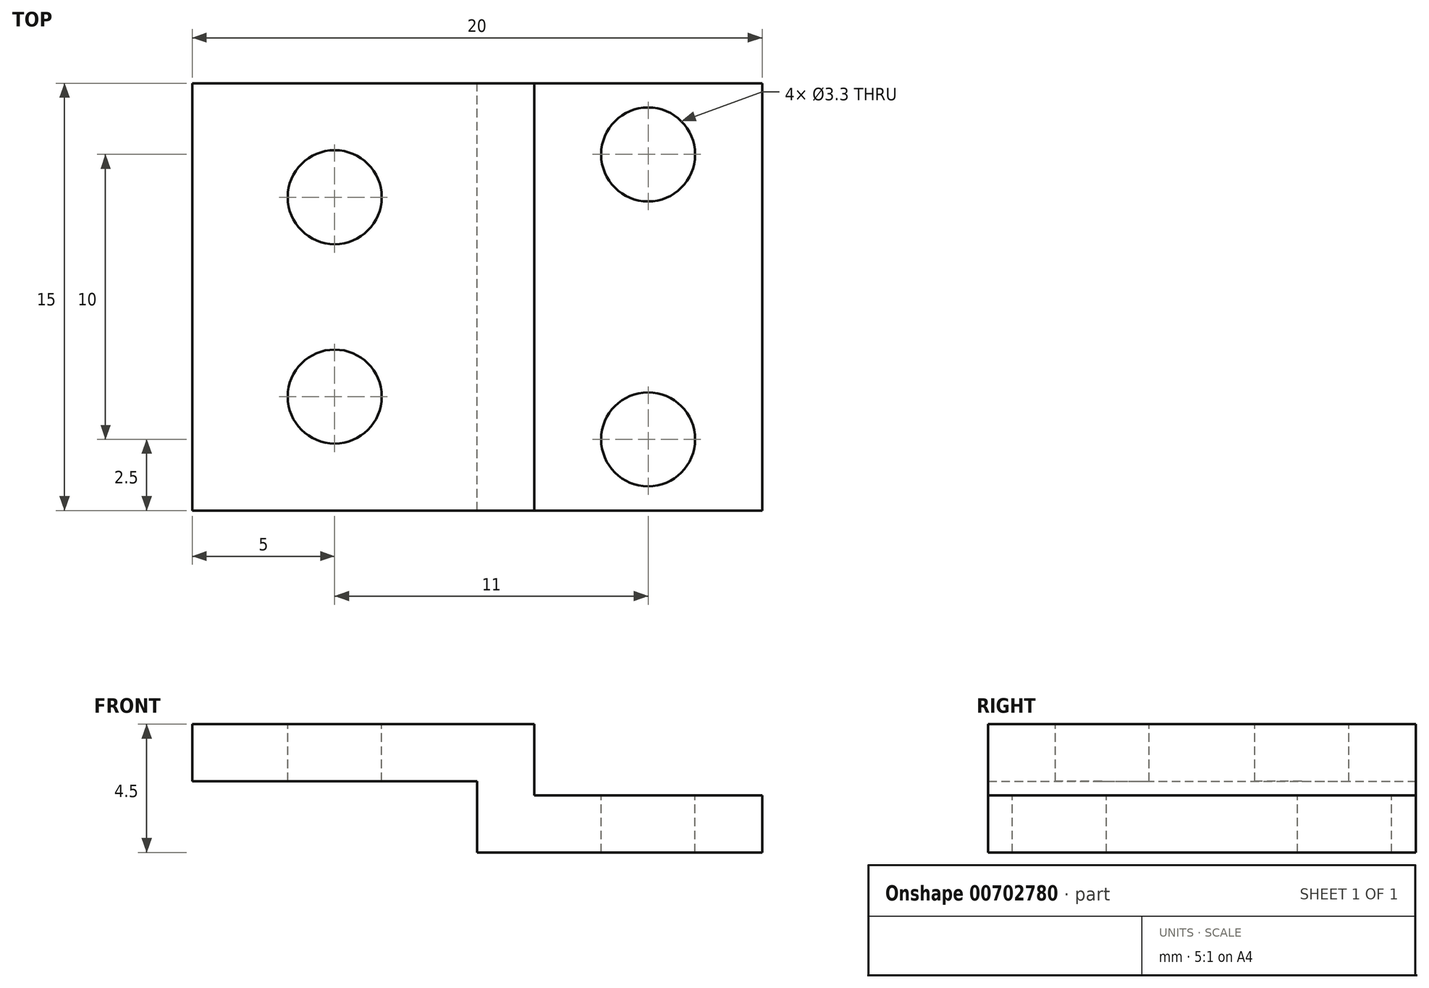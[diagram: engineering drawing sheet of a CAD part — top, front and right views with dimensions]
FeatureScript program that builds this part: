
annotation { "Feature Type Name" : "Feature", "Feature Type Description" : "" }
export const myFeature = defineFeature(function(context is Context, id is Id, definition is map)
    precondition{}
    {
        {
            var Q0;
            Q0=qCreatedBy(makeId("Front.planeOp"),FACE);
            var sketch = newSketch(context, id + "F0", { "sketchPlane" : qUnion([Q0])});
            skLineSegment(sketch, "E0", {"start": v(0, 0) * mm, "end": v(-8, 0) * mm});
            skLineSegment(sketch, "E1", {"start": v(-8, 0) * mm, "end": v(-8, 2.5) * mm});
            skLineSegment(sketch, "E2", {"start": v(-8, 2.5) * mm, "end": v(-20, 2.5) * mm});
            skLineSegment(sketch, "E3.0", {"start": v(-10, 0.5) * mm, "end": v(-20, 0.5) * mm});
            skLineSegment(sketch, "E3.1", {"start": v(-10, -2) * mm, "end": v(-10, 0.5) * mm});
            skLineSegment(sketch, "E3.2", {"start": v(0, -2) * mm, "end": v(-10, -2) * mm});
            skLineSegment(sketch, "E4", {"start": v(-20, 2.5) * mm, "end": v(-20, 0.5) * mm});
            skLineSegment(sketch, "E5", {"start": v(0, -2) * mm, "end": v(0, 0) * mm});
            skSolve(sketch);
        }
        {
            var Q0;
            Q0 = qSketchRegion(id + "F0", true);
            extrude(context, id + "F1", {"entities" : qUnion([Q0]), "endBound" : BoundingType.SYMMETRIC, "depth" : 15 * mm, "offsetDistance" : 25 * mm});
        }
        {
            var Q0;
            Q0=makeQuery(id+"F1.opExtrude","SWEPT_FACE",FACE,{"disambiguationData":[OSD([sQuery(id+"F0.wireOp",EDGE,"E2")])]});
            var sketch = newSketch(context, id + "F2", { "sketchPlane" : qUnion([Q0])});
            skLineSegment(sketch, "E6", {"start": v(-20, 7.5) * mm, "end": v(-20, -7.5) * mm});
            skLineSegment(sketch, "E7", {"start": v(-20, 0) * mm, "end": v(-8, 0) * mm, "construction": true});
            skLineSegment(sketch, "E8", {"start": v(-20, -3.5) * mm, "end": v(-8, -3.5) * mm, "construction": true});
            skLineSegment(sketch, "E9", {"start": v(-15, -7.5) * mm, "end": v(-15, 7.5) * mm, "construction": true});
            skCircle(sketch, "E10", {"center": v(-15, -3.5) * mm, "radius": 1.55 * mm, "construction": true});
            skCircle(sketch, "E11.MirrorC", {"center": v(-15, 3.5) * mm, "radius": 1.55 * mm, "construction": true});
            skLineSegment(sketch, "E12.MirrorCS", {"start": v(-20, 3.5) * mm, "end": v(-8, 3.5) * mm, "construction": true});
            skSolve(sketch);
        }
        {
            var Q0;
            Q0=sQuery(id+"F2.wireOp",VERTEX,"E10.center");
            var Q1;
            Q1=sQuery(id+"F2.wireOp",VERTEX,"E11.MirrorC.center");
            var Q2;
            Q2=makeQuery(id+"F1.opExtrude","SWEPT_BODY",BODY,{"disambiguationData":[OSD([sQuery(id+"F0.wireOp",EDGE,"E0"),sQuery(id+"F0.wireOp",EDGE,"E1"),sQuery(id+"F0.wireOp",EDGE,"E2"),sQuery(id+"F0.wireOp",EDGE,"E3.0"),sQuery(id+"F0.wireOp",EDGE,"E3.1"),sQuery(id+"F0.wireOp",EDGE,"E3.2"),sQuery(id+"F0.wireOp",EDGE,"E4"),sQuery(id+"F0.wireOp",EDGE,"E5")])]});
            hole(context, id + "F3", {"style" : HoleStyle.SIMPLE, "endStyle" : HoleEndStyle.THROUGH, "standardTappedOrClearance" : lookupTablePath({ "standard" : "ISO", "fit" : "Normal", "size" : "M3", "type" : "Clearance" }), "standardBlindInLast" : lookupTablePath({ "fit" : "Standard", "standard" : "ISO", "size" : "M3", "type" : "Clearance" }), "holeDiameter" : 3.3 * mm, "majorDiameter" : 5 * mm, "isTappedThrough" : true, "tappedDepth" : 12 * mm, "tapClearance" : 3, "locations" : qUnion([Q0, Q1]), "scope" : qUnion([Q2])});
        }
        {
            var Q0;
            Q0=makeQuery(id+"F1.opExtrude","SWEPT_FACE",FACE,{"disambiguationData":[OSD([sQuery(id+"F0.wireOp",EDGE,"E0")])]});
            var sketch = newSketch(context, id + "F4", { "sketchPlane" : qUnion([Q0])});
            skLineSegment(sketch, "E13", {"start": v(0, -7.5) * mm, "end": v(0, 7.5) * mm, "construction": true});
            skLineSegment(sketch, "E14.0", {"start": v(-4, -7.5) * mm, "end": v(-4, 7.5) * mm, "construction": true});
            skLineSegment(sketch, "E15", {"start": v(0, 0) * mm, "end": v(-8, 0) * mm, "construction": true});
            skLineSegment(sketch, "E16", {"start": v(0, -5) * mm, "end": v(-7.64, -5) * mm, "construction": true});
            skCircle(sketch, "E17", {"center": v(-4, -5) * mm, "radius": 1.55 * mm, "construction": true});
            skCircle(sketch, "E18.MirrorC", {"center": v(-4, 5) * mm, "radius": 1.55 * mm, "construction": true});
            skLineSegment(sketch, "E19.MirrorCS", {"start": v(0, 5) * mm, "end": v(-7.64, 5) * mm, "construction": true});
            skSolve(sketch);
        }
        {
            var Q0;
            Q0=sQuery(id+"F4.wireOp",VERTEX,"E17.center");
            var Q1;
            Q1=sQuery(id+"F4.wireOp",VERTEX,"E18.MirrorC.center");
            var Q2;
            Q2=makeQuery(id+"F1.opExtrude","SWEPT_BODY",BODY,{"disambiguationData":[OSD([sQuery(id+"F0.wireOp",EDGE,"E0"),sQuery(id+"F0.wireOp",EDGE,"E1"),sQuery(id+"F0.wireOp",EDGE,"E2"),sQuery(id+"F0.wireOp",EDGE,"E3.0"),sQuery(id+"F0.wireOp",EDGE,"E3.1"),sQuery(id+"F0.wireOp",EDGE,"E3.2"),sQuery(id+"F0.wireOp",EDGE,"E4"),sQuery(id+"F0.wireOp",EDGE,"E5")])]});
            hole(context, id + "F5", {"style" : HoleStyle.SIMPLE, "endStyle" : HoleEndStyle.THROUGH, "standardTappedOrClearance" : lookupTablePath({ "standard" : "ISO", "fit" : "Normal", "size" : "M3", "type" : "Clearance" }), "standardBlindInLast" : lookupTablePath({ "fit" : "Standard", "standard" : "ISO", "size" : "M3", "type" : "Clearance" }), "holeDiameter" : 3.3 * mm, "majorDiameter" : 5 * mm, "isTappedThrough" : true, "tappedDepth" : 12 * mm, "tapClearance" : 3, "locations" : qUnion([Q0, Q1]), "scope" : qUnion([Q2])});
        }
    });
